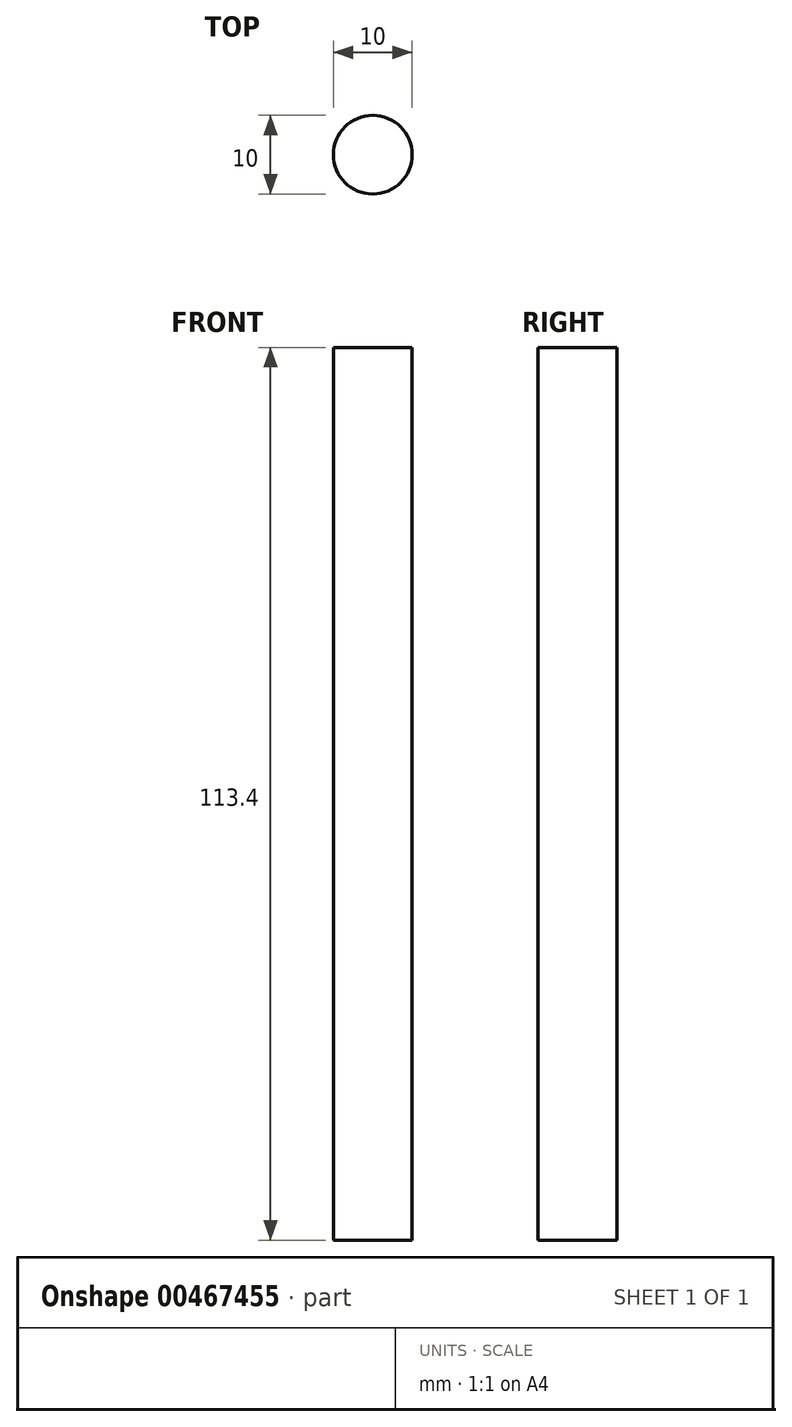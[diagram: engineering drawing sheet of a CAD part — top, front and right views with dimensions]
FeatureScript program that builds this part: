
annotation { "Feature Type Name" : "Feature", "Feature Type Description" : "" }
export const myFeature = defineFeature(function(context is Context, id is Id, definition is map)
    precondition{}
    {
        {
            var Q0;
            Q0=qCreatedBy(makeId("Top.planeOp"),FACE);
            var sketch = newSketch(context, id + "F0", { "sketchPlane" : qUnion([Q0])});
            skCircle(sketch, "E0", {"center": v(0, 0) * mm, "radius": 5 * mm});
            skSolve(sketch);
        }
        {
            var Q0;
            Q0=makeQuery(id+"F0.imprint","IMPRINT",FACE,{"disambiguationData":[TD([[makeQuery(id+"F0.imprint","IMPRINT",EDGE,{"derivedFrom":sQuery(id+"F0.wireOp",EDGE,"E0")}),1.0]])]});
            extrude(context, id + "F1", {"entities" : qUnion([Q0]), "depth" : 113.4 * mm});
        }
    });
